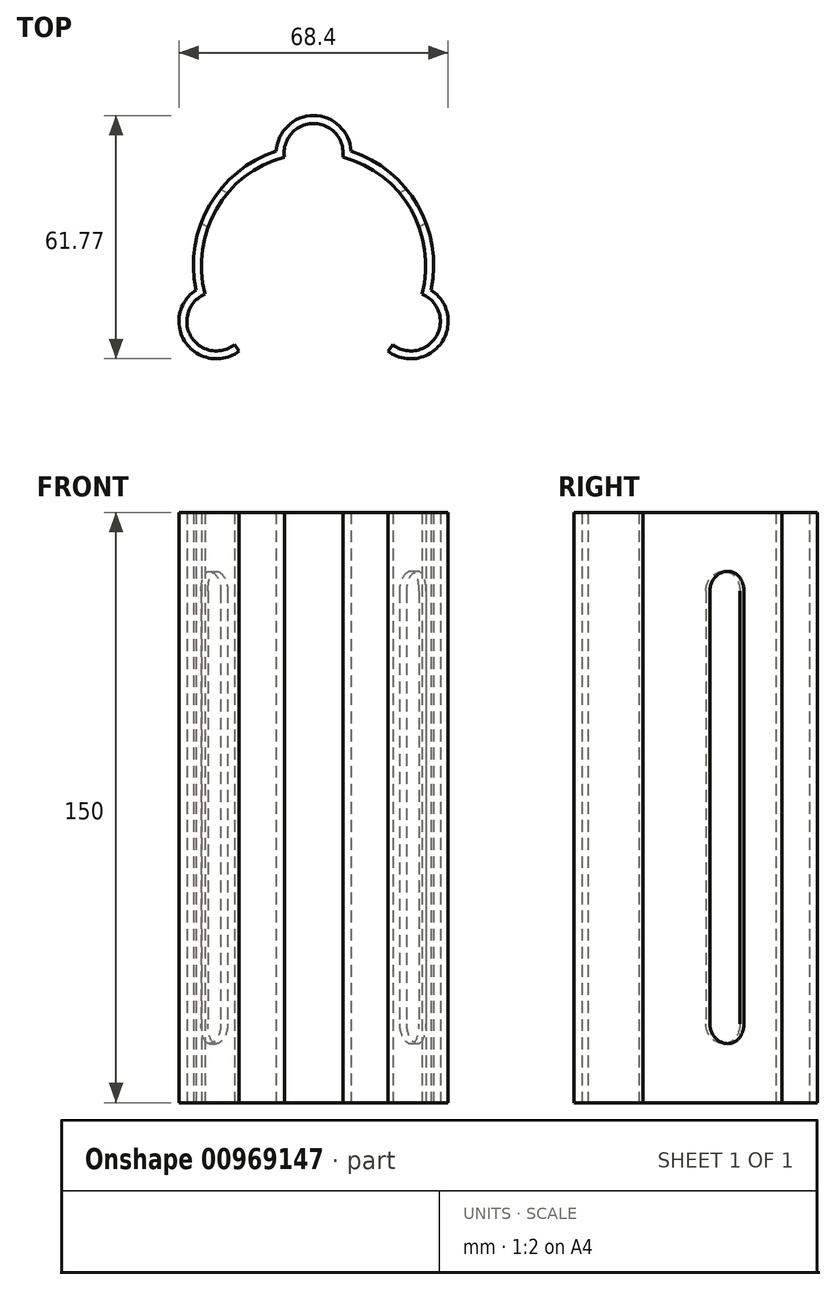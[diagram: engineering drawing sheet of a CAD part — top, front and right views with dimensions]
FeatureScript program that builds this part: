
annotation { "Feature Type Name" : "Feature", "Feature Type Description" : "" }
export const myFeature = defineFeature(function(context is Context, id is Id, definition is map)
    precondition{}
    {
        {
            var Q0;
            Q0=qCreatedBy(makeId("Top.planeOp"),FACE);
            var sketch = newSketch(context, id + "F0", { "sketchPlane" : qUnion([Q0])});
            skArc(sketch, "E0", {"start": v(-27.56, 6.93) * mm, "mid": v(-31.2, -3.75) * mm, "end": v(-20.12, -5.95) * mm});
            skArc(sketch, "E1", {"start": v(20.12, -5.95) * mm, "mid": v(31.2, -3.75) * mm, "end": v(27.56, 6.93) * mm});
            skArc(sketch, "E2", {"start": v(7.43, 41.79) * mm, "mid": v(0, 50.27) * mm, "end": v(-7.43, 41.79) * mm});
            skCircle(sketch, "E3", {"center": v(0, 14.26) * mm, "radius": 21.02 * mm, "construction": true});
            skArc(sketch, "E4", {"start": v(27.56, 6.93) * mm, "mid": v(24.7, 28.52) * mm, "end": v(7.43, 41.79) * mm});
            skArc(sketch, "E5.trimOffspring", {"start": v(-7.43, 41.79) * mm, "mid": v(-24.7, 28.52) * mm, "end": v(-27.56, 6.93) * mm});
            skArc(sketch, "E6.0", {"start": v(-29.86, 7.97) * mm, "mid": v(-32.45, -5.48) * mm, "end": v(-18.9, -7.53) * mm});
            skArc(sketch, "E6.1", {"start": v(18.9, -7.53) * mm, "mid": v(32.45, -5.48) * mm, "end": v(29.86, 7.97) * mm});
            skArc(sketch, "E6.2", {"start": v(29.86, 7.97) * mm, "mid": v(26.43, 29.52) * mm, "end": v(9.49, 43.26) * mm});
            skArc(sketch, "E6.3", {"start": v(9.49, 43.26) * mm, "mid": v(0, 52.27) * mm, "end": v(-9.49, 43.26) * mm});
            skArc(sketch, "E6.4", {"start": v(-9.49, 43.26) * mm, "mid": v(-26.43, 29.52) * mm, "end": v(-29.86, 7.97) * mm});
            skLineSegment(sketch, "E7", {"start": v(-20.12, -5.95) * mm, "end": v(-18.9, -7.53) * mm});
            skLineSegment(sketch, "E8", {"start": v(18.9, -7.53) * mm, "end": v(20.12, -5.95) * mm});
            skSolve(sketch);
        }
        {
            var Q0;
            Q0 = qSketchRegion(id + "F0", true);
            extrude(context, id + "F1", {"entities" : qUnion([Q0]), "depth" : 150 * mm, "offsetDistance" : 25 * mm});
        }
        {
            var Q0;
            Q0=makeQuery(id+"F1.opExtrude","CAP_VERTEX",VERTEX,{"disambiguationData":[OSD([sQuery(id+"F0.wireOp",EDGE,"E6.2"),sQuery(id+"F0.wireOp",EDGE,"E6.3")])],"isStart":false});
            var Q1;
            Q1=makeQuery(id+"F1.opExtrude","CAP_VERTEX",VERTEX,{"disambiguationData":[OSD([sQuery(id+"F0.wireOp",EDGE,"E6.1"),sQuery(id+"F0.wireOp",EDGE,"E6.2")])],"isStart":false});
            var Q2;
            Q2=makeQuery(id+"F1.opExtrude","CAP_VERTEX",VERTEX,{"disambiguationData":[OSD([sQuery(id+"F0.wireOp",EDGE,"E6.1"),sQuery(id+"F0.wireOp",EDGE,"E6.2")])],"isStart":true});
            cPlane(context, id + "F2", {"entities" : qUnion([Q0, Q1, Q2]), "cplaneType" : CPlaneType.THREE_POINT, "offset" : 25 * mm, "width" : 150 * mm, "height" : 150 * mm});
        }
        {
            var Q0;
            Q0=qCreatedBy(id+"F2.planeOp",FACE);
            var sketch = newSketch(context, id + "F3", { "sketchPlane" : qUnion([Q0])});
            skLineSegment(sketch, "E9.0", {"start": v(8.03, 150) * mm, "end": v(8.03, 0) * mm, "construction": true});
            skLineSegment(sketch, "E10.0", {"start": v(-32.72, 150) * mm, "end": v(-32.72, 0) * mm, "construction": true});
            skLineSegment(sketch, "E11.bottom", {"start": v(-12.35, 135) * mm, "end": v(-12.35, 135) * mm});
            skLineSegment(sketch, "E11.top", {"start": v(-12.35, 15) * mm, "end": v(-12.35, 15) * mm});
            skLineSegment(sketch, "E11.left", {"start": v(-7.35, 130) * mm, "end": v(-7.35, 20) * mm});
            skLineSegment(sketch, "E11.right", {"start": v(-17.35, 130) * mm, "end": v(-17.35, 20) * mm});
            skPoint(sketch, "E12.0", {"position": v(-12.35, 150) * mm});
            skLineSegment(sketch, "E13", {"start": v(-12.35, 150) * mm, "end": v(-12.35, 0) * mm, "construction": true});
            skPoint(sketch, "E14.visualSharp", {"position": v(-7.35, 135) * mm});
            skArc(sketch, "E14.filletArc", {"start": v(-7.35, 130) * mm, "mid": v(-8.81, 133.54) * mm, "end": v(-12.35, 135) * mm});
            skPoint(sketch, "E15.visualSharp", {"position": v(-7.35, 15) * mm});
            skArc(sketch, "E15.filletArc", {"start": v(-12.35, 15) * mm, "mid": v(-8.81, 16.46) * mm, "end": v(-7.35, 20) * mm});
            skPoint(sketch, "E16.visualSharp", {"position": v(-17.35, 15) * mm});
            skArc(sketch, "E16.filletArc", {"start": v(-17.35, 20) * mm, "mid": v(-15.88, 16.46) * mm, "end": v(-12.35, 15) * mm});
            skPoint(sketch, "E17.visualSharp", {"position": v(-17.35, 135) * mm});
            skArc(sketch, "E17.filletArc", {"start": v(-12.35, 135) * mm, "mid": v(-15.88, 133.54) * mm, "end": v(-17.35, 130) * mm});
            skSolve(sketch);
        }
        {
            var Q0;
            Q0 = qSketchRegion(id + "F3", true);
            var Q1;
            Q1=makeQuery(id+"F1.opExtrude","SWEPT_BODY",BODY,{"disambiguationData":[OSD([sQuery(id+"F0.wireOp",EDGE,"E0"),sQuery(id+"F0.wireOp",EDGE,"E1"),sQuery(id+"F0.wireOp",EDGE,"E2"),sQuery(id+"F0.wireOp",EDGE,"E4"),sQuery(id+"F0.wireOp",EDGE,"E5.trimOffspring"),sQuery(id+"F0.wireOp",EDGE,"E6.0"),sQuery(id+"F0.wireOp",EDGE,"E6.1"),sQuery(id+"F0.wireOp",EDGE,"E6.2"),sQuery(id+"F0.wireOp",EDGE,"E6.3"),sQuery(id+"F0.wireOp",EDGE,"E6.4"),sQuery(id+"F0.wireOp",EDGE,"E7"),sQuery(id+"F0.wireOp",EDGE,"E8")])]});
            extrude(context, id + "F4", {"entities" : qUnion([Q0]), "operationType" : NewBodyOperationType.REMOVE, "oppositeDirection" : true, "depth" : 14.6 * mm, "endBoundEntityBody" : qUnion([Q1]), "offsetDistance" : 25 * mm});
        }
        {
            var Q0;
            Q0=makeQuery(id+"F1.opExtrude","CAP_VERTEX",VERTEX,{"disambiguationData":[OSD([sQuery(id+"F0.wireOp",EDGE,"E6.3"),sQuery(id+"F0.wireOp",EDGE,"E6.4")])],"isStart":false});
            var Q1;
            Q1=makeQuery(id+"F1.opExtrude","CAP_VERTEX",VERTEX,{"disambiguationData":[OSD([sQuery(id+"F0.wireOp",EDGE,"E6.0"),sQuery(id+"F0.wireOp",EDGE,"E6.4")])],"isStart":false});
            var Q2;
            Q2=makeQuery(id+"F1.opExtrude","CAP_VERTEX",VERTEX,{"disambiguationData":[OSD([sQuery(id+"F0.wireOp",EDGE,"E6.0"),sQuery(id+"F0.wireOp",EDGE,"E6.4")])],"isStart":true});
            cPlane(context, id + "F5", {"entities" : qUnion([Q0, Q1, Q2]), "cplaneType" : CPlaneType.THREE_POINT, "offset" : 25 * mm, "width" : 150 * mm, "height" : 150 * mm});
        }
        {
            var Q0;
            Q0=qCreatedBy(id+"F5.planeOp",FACE);
            var sketch = newSketch(context, id + "F6", { "sketchPlane" : qUnion([Q0])});
            skPoint(sketch, "E18.0", {"position": v(-12.35, 150) * mm});
            skPoint(sketch, "E19.0", {"position": v(-32.72, 150) * mm});
            skLineSegment(sketch, "E20", {"start": v(-12.35, 150) * mm, "end": v(-12.35, -11.68) * mm, "construction": true});
            skLineSegment(sketch, "E21.bottom", {"start": v(-12.35, 135) * mm, "end": v(-12.35, 135) * mm});
            skLineSegment(sketch, "E21.top", {"start": v(-12.35, 15) * mm, "end": v(-12.35, 15) * mm});
            skLineSegment(sketch, "E21.left", {"start": v(-17.35, 130) * mm, "end": v(-17.35, 20) * mm});
            skLineSegment(sketch, "E21.right", {"start": v(-7.35, 130) * mm, "end": v(-7.35, 20) * mm});
            skPoint(sketch, "E22.visualSharp", {"position": v(-17.35, 135) * mm});
            skArc(sketch, "E22.filletArc", {"start": v(-12.35, 135) * mm, "mid": v(-15.88, 133.54) * mm, "end": v(-17.35, 130) * mm});
            skPoint(sketch, "E23.visualSharp", {"position": v(-17.35, 15) * mm});
            skArc(sketch, "E23.filletArc", {"start": v(-17.35, 20) * mm, "mid": v(-15.88, 16.46) * mm, "end": v(-12.35, 15) * mm});
            skPoint(sketch, "E24.visualSharp", {"position": v(-7.35, 15) * mm});
            skArc(sketch, "E24.filletArc", {"start": v(-12.35, 15) * mm, "mid": v(-8.81, 16.46) * mm, "end": v(-7.35, 20) * mm});
            skPoint(sketch, "E25.visualSharp", {"position": v(-7.35, 135) * mm});
            skArc(sketch, "E25.filletArc", {"start": v(-7.35, 130) * mm, "mid": v(-8.81, 133.54) * mm, "end": v(-12.35, 135) * mm});
            skSolve(sketch);
        }
        {
            var Q0;
            Q0 = qSketchRegion(id + "F6", true);
            extrude(context, id + "F7", {"entities" : qUnion([Q0]), "operationType" : NewBodyOperationType.REMOVE, "depth" : 25 * mm, "offsetDistance" : 25 * mm});
        }
    });
